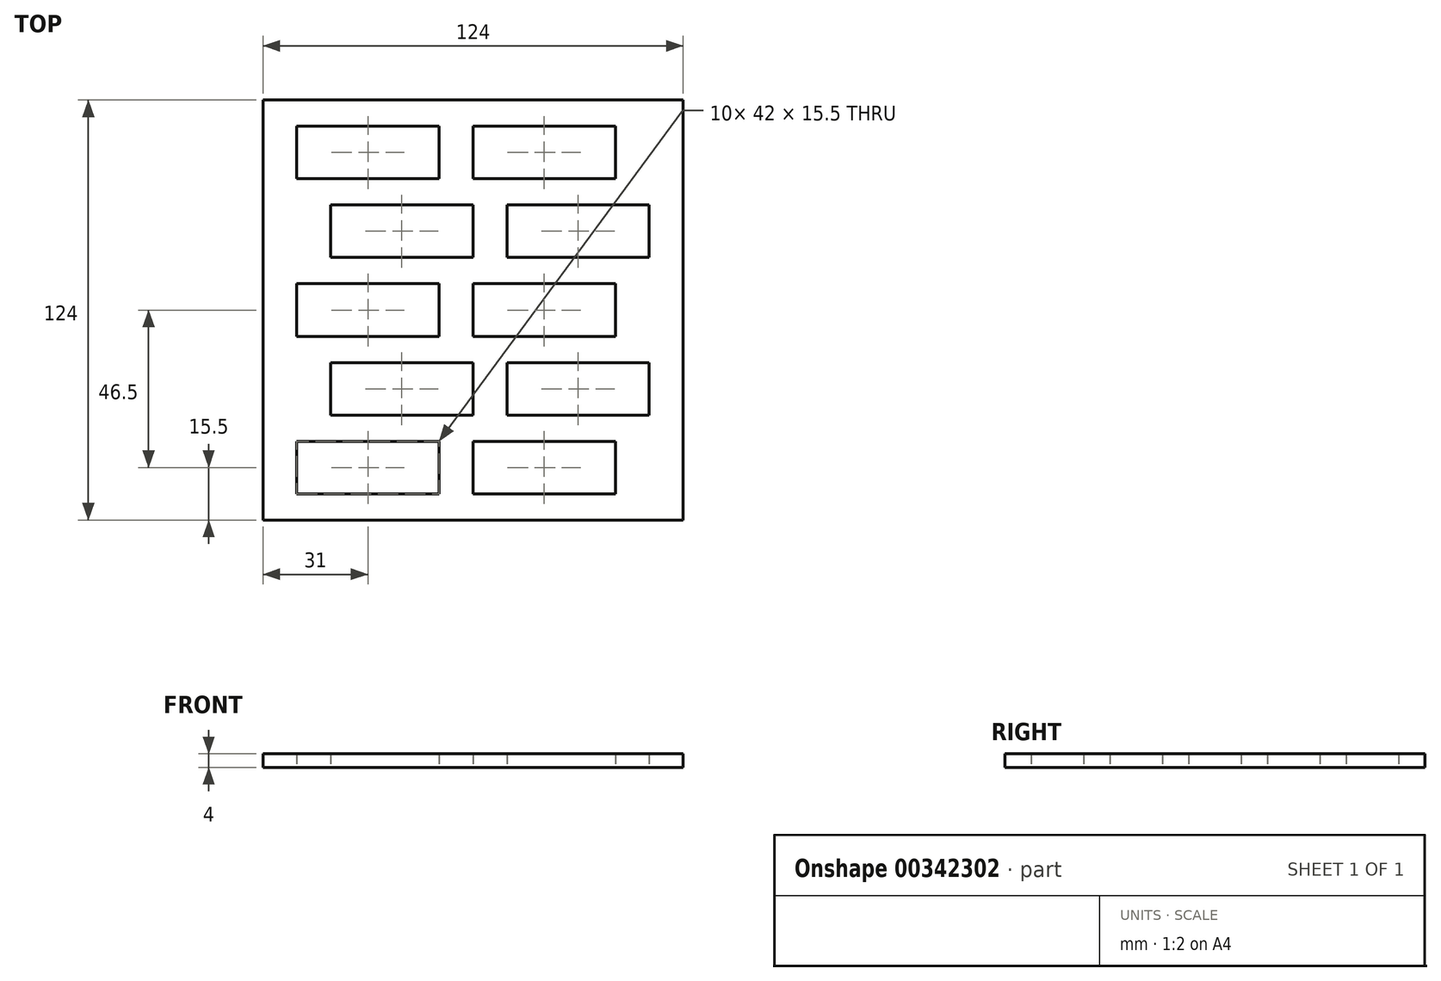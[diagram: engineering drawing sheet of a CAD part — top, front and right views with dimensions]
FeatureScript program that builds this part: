
annotation { "Feature Type Name" : "Feature", "Feature Type Description" : "" }
export const myFeature = defineFeature(function(context is Context, id is Id, definition is map)
    precondition{}
    {
        {
            var Q0;
            Q0=qCreatedBy(makeId("Top.planeOp"),FACE);
            var sketch = newSketch(context, id + "F0", { "sketchPlane" : qUnion([Q0])});
            skLineSegment(sketch, "E0.bottom", {"start": v(62, -62) * mm, "end": v(-62, -62) * mm});
            skLineSegment(sketch, "E0.top", {"start": v(62, 62) * mm, "end": v(-62, 62) * mm});
            skLineSegment(sketch, "E0.left", {"start": v(62, -62) * mm, "end": v(62, 62) * mm});
            skLineSegment(sketch, "E0.right", {"start": v(-62, -62) * mm, "end": v(-62, 62) * mm});
            skPoint(sketch, "E0.middle", {"position": v(0, 0) * mm});
            skLineSegment(sketch, "E1.bottom", {"start": v(-52, 54.25) * mm, "end": v(-10, 54.25) * mm});
            skLineSegment(sketch, "E1.top", {"start": v(-52, 38.75) * mm, "end": v(-10, 38.75) * mm});
            skLineSegment(sketch, "E1.left", {"start": v(-52, 54.25) * mm, "end": v(-52, 38.75) * mm});
            skLineSegment(sketch, "E1.right", {"start": v(-10, 54.25) * mm, "end": v(-10, 38.75) * mm});
            skLineSegment(sketch, "E2.direction1", {"start": v(-52, 38.75) * mm, "end": v(0, 38.75) * mm, "construction": true});
            skLineSegment(sketch, "E3.bottom", {"start": v(52, 31) * mm, "end": v(10, 31) * mm});
            skLineSegment(sketch, "E3.top", {"start": v(52, 15.5) * mm, "end": v(10, 15.5) * mm});
            skLineSegment(sketch, "E3.left", {"start": v(52, 31) * mm, "end": v(52, 15.5) * mm});
            skLineSegment(sketch, "E3.right", {"start": v(10, 31) * mm, "end": v(10, 15.5) * mm});
            skLineSegment(sketch, "E4.1.0.0", {"start": v(0, 15.5) * mm, "end": v(-42, 15.5) * mm});
            skLineSegment(sketch, "E4.1.0.1", {"start": v(0, 31) * mm, "end": v(0, 15.5) * mm});
            skLineSegment(sketch, "E4.1.0.2", {"start": v(0, 31) * mm, "end": v(-42, 31) * mm});
            skLineSegment(sketch, "E4.1.0.3", {"start": v(-42, 31) * mm, "end": v(-42, 15.5) * mm});
            skLineSegment(sketch, "E4.direction1", {"start": v(10, 15.5) * mm, "end": v(-42, 15.5) * mm, "construction": true});
            skLineSegment(sketch, "E5.0.1.0", {"start": v(0, 54.25) * mm, "end": v(0, 38.75) * mm});
            skLineSegment(sketch, "E5.3.1.0", {"start": v(42, 54.25) * mm, "end": v(42, 38.75) * mm});
            skLineSegment(sketch, "E5.6.1.0", {"start": v(0, 54.25) * mm, "end": v(42, 54.25) * mm});
            skLineSegment(sketch, "E5.9.1.0", {"start": v(0, 38.75) * mm, "end": v(42, 38.75) * mm});
            skLineSegment(sketch, "E6.0.1.0", {"start": v(-10, 7.75) * mm, "end": v(-10, -7.75) * mm});
            skLineSegment(sketch, "E6.0.1.1", {"start": v(-52, 7.75) * mm, "end": v(-52, -7.75) * mm});
            skLineSegment(sketch, "E6.0.1.2", {"start": v(-52, 7.75) * mm, "end": v(-10, 7.75) * mm});
            skLineSegment(sketch, "E6.0.1.3", {"start": v(-52, -7.75) * mm, "end": v(0, -7.75) * mm, "construction": true});
            skLineSegment(sketch, "E6.0.1.4", {"start": v(0, 7.75) * mm, "end": v(42, 7.75) * mm});
            skLineSegment(sketch, "E6.0.1.5", {"start": v(0, 7.75) * mm, "end": v(0, -7.75) * mm});
            skLineSegment(sketch, "E6.0.1.6", {"start": v(0, -7.75) * mm, "end": v(42, -7.75) * mm});
            skLineSegment(sketch, "E6.0.1.7", {"start": v(42, 7.75) * mm, "end": v(42, -7.75) * mm});
            skLineSegment(sketch, "E6.0.1.8", {"start": v(-52, -7.75) * mm, "end": v(-10, -7.75) * mm});
            skLineSegment(sketch, "E6.0.2.0", {"start": v(-10, -38.75) * mm, "end": v(-10, -54.25) * mm});
            skLineSegment(sketch, "E6.0.2.1", {"start": v(-52, -38.75) * mm, "end": v(-52, -54.25) * mm});
            skLineSegment(sketch, "E6.0.2.2", {"start": v(-52, -38.75) * mm, "end": v(-10, -38.75) * mm});
            skLineSegment(sketch, "E6.0.2.3", {"start": v(-52, -54.25) * mm, "end": v(0, -54.25) * mm, "construction": true});
            skLineSegment(sketch, "E6.0.2.4", {"start": v(0, -38.75) * mm, "end": v(42, -38.75) * mm});
            skLineSegment(sketch, "E6.0.2.5", {"start": v(0, -38.75) * mm, "end": v(0, -54.25) * mm});
            skLineSegment(sketch, "E6.0.2.6", {"start": v(0, -54.25) * mm, "end": v(42, -54.25) * mm});
            skLineSegment(sketch, "E6.0.2.7", {"start": v(42, -38.75) * mm, "end": v(42, -54.25) * mm});
            skLineSegment(sketch, "E6.0.2.8", {"start": v(-52, -54.25) * mm, "end": v(-10, -54.25) * mm});
            skLineSegment(sketch, "E6.direction1", {"start": v(-52, 38.75) * mm, "end": v(-27, 38.75) * mm, "construction": true});
            skLineSegment(sketch, "E6.direction2", {"start": v(-52, 38.75) * mm, "end": v(-52, -7.75) * mm, "construction": true});
            skLineSegment(sketch, "E7.0.1.0", {"start": v(10, -15.5) * mm, "end": v(10, -31) * mm});
            skLineSegment(sketch, "E7.0.1.1", {"start": v(0, -15.5) * mm, "end": v(-42, -15.5) * mm});
            skLineSegment(sketch, "E7.0.1.2", {"start": v(52, -15.5) * mm, "end": v(52, -31) * mm});
            skLineSegment(sketch, "E7.0.1.3", {"start": v(52, -31) * mm, "end": v(10, -31) * mm});
            skLineSegment(sketch, "E7.0.1.4", {"start": v(0, -15.5) * mm, "end": v(0, -31) * mm});
            skLineSegment(sketch, "E7.0.1.5", {"start": v(-42, -15.5) * mm, "end": v(-42, -31) * mm});
            skLineSegment(sketch, "E7.0.1.6", {"start": v(10, -31) * mm, "end": v(-42, -31) * mm, "construction": true});
            skLineSegment(sketch, "E7.0.1.7", {"start": v(52, -15.5) * mm, "end": v(10, -15.5) * mm});
            skLineSegment(sketch, "E7.0.1.8", {"start": v(0, -31) * mm, "end": v(-42, -31) * mm});
            skLineSegment(sketch, "E7.direction1", {"start": v(-42, 15.5) * mm, "end": v(-17, 15.5) * mm, "construction": true});
            skLineSegment(sketch, "E7.direction2", {"start": v(-42, 15.5) * mm, "end": v(-42, -31) * mm, "construction": true});
            skSolve(sketch);
        }
        {
            var Q0;
            Q0 = qSketchRegion(id + "F0", true);
            extrude(context, id + "F1", {"entities" : qUnion([Q0]), "endBound" : BoundingType.SYMMETRIC, "depth" : 4 * mm});
        }
    });
